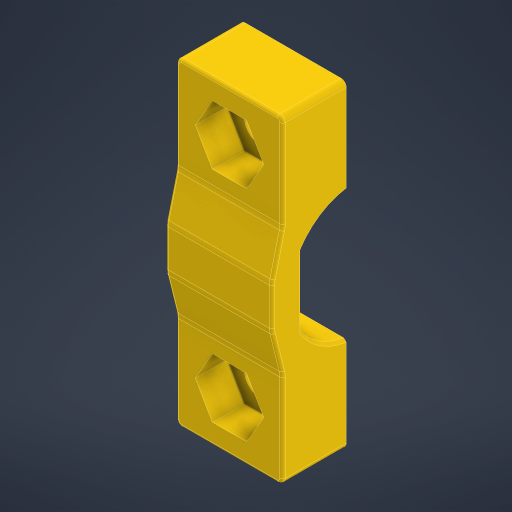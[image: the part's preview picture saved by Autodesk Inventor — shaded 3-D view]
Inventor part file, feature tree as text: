
AUTODESK INVENTOR PART (.ipt)
format: ipt  version: 2024 (Build 280153000, 153)  size: 352,256 bytes
history: native  units: in
note: dims shown in document units (in); Inventor stores cm internally (conversion verified against a paired STEP export)
features: sketch x6, extrude x4, projected_geometry x4, fillet x3, other x1, chamfer x1
ambient origin geometry x8: Origin, YZ Plane, XZ Plane, XY Plane, X Axis, Y Axis, Z Axis, Center Point
bodies: Body1 (feature_tree)
feature tree (19):
  other  "Těleso1"
  extrude  "Vysunutí1"  Depth=1.1811in
  extrude  "Vysunutí2"  Depth=0.3937in
  extrude  "Vysunutí5"  Depth=0.126in
  fillet  "Zaoblení1"  Radius=0.3937in
  fillet  "Zaoblení2"  [1 undecoded]
  chamfer  "Zkosení1"  Distance=0.1181in
  fillet  "Zaoblení3"  Radius=0.1181in
  sketch  "Náčrt4"
  sketch  "Náčrt5"
  extrude  "Vysunutí4"  Depth=0.0787in
  sketch  "Náčrt1"
  sketch  "Náčrt2"
  sketch  "Náčrt6"
  sketch  "Náčrt7"
  projected_geometry  "Promítnutá smyčka3"
  projected_geometry  "Promítnutá smyčka4"
  projected_geometry  "Promítnutá smyčka5"
  projected_geometry  "Promítnutá smyčka6"
note: 1 required parameter value undecoded (feature->parameter linkage not recoverable at this tier; creation-order binding heuristic only, values carry confidence <= 0.55)
